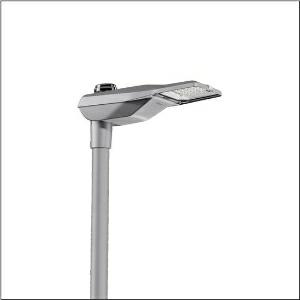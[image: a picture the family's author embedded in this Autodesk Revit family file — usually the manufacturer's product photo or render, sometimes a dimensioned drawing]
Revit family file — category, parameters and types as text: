
# Revit family: streetlight_sl_21_micro___st1_5a_5xe5p47n08cb_4c70
name_source: partatom
category: Lighting Fixtures
units: mm (PartAtom-declared; Revit-internal decimal feet)

## family parameters
Cut with Voids When Loaded = No
Host = Face
Light Source = No
Part Type = Normal
Room Calculation Point = No
Round Connector Dimension = Use Diameter
Shared = No

## types (1)
- --- (1 x LED, 2340 lm, 15.8 W, 4000K)
    Apparent Load = 16 VA
    CIE Flux Codes = 22 53 95 100 100
    Color Rendering = 70
    Color Temperature = 4000K
    Default Elevation = 1800 mm
    Description = Streetlight SL 21 micro, mast luminaire, primary light control with lens, of PMMA, primary optical cover: cover, of toughened safety glass, transparent, light distribution: ST1.5a, light emission: direct distribution, primary light characteristic: asymmetric, installation type: post-top, LED, 3G 1.5mm², High Power LED, rated luminous flux: 2.340lm, luminous efficacy: 148lm/W, light colour: 740, colour temperature: 4000K, control gear: NEMA (7pin), control: overheat protection, pre-setting: linear dimming characteristic, constant luminous flux control, time-dependent luminous flux control, flexible luminous flux parameterisation, mains connection: 230..240V, AC, 50/60Hz, connection cable pre-assembled, cable length: 6,5m, wiring characteristics: H07RN-F, start of lifetime: 16W, end of service life: 16W, reduction: 8W, luminaire housing, of diecast aluminium (EN AC-44300), powder-coated, SITECO metallic grey (DB 702S), corrosivity category C5 high according to DIN EN ISO 12944, multi-level sealing system, sealing non-destructively replaceable, inclination adjustable: 0°, 5°, 10°, 15°, length: 528mm, width: 235mm, height: 110mm, spigot size: 76/60mm (post-top), mounting height: 4..8m, protection rating (complete): IP66, insulation class (complete): insulation class I (protective earthing), certification: CE, ENEC, ENEC+, VDE, impact resistance: IK10, permissible operating ambient temperature for outdoor applications: -40..+50°C, standard-compliant lighting for roads and squares, packaging unit: 1 piece

Light Distribution: ST1.5a
    Height = 110 mm
    Lamp = 1 x LED
    Lamp Light Flux = 2340 lm
    Lamp Power = 15.8 W
    Lamp count = 1
    Length = 528 mm
    Luminous efficacy = 148 lm/W
    Manufacturer = Siteco
    ModVariant = No
    Model = 5XE5P47N08CB
    Number of Poles = 1
    OnlyDefault = Yes
    Power Factor = 1
    Product Name = Streetlight SL 21 micro | ST1.5a
    Product group = mast luminaire | pylon top
    ProductGroupID = 6100
    Protection Class = Protection class I
    Protection Degree = IP 66
    RLX_Detail_Level = 1
    RLX_Emergency_Light_Flux = 0 lm
    RLX_Emergency_Type = 0
    RLX_Emergency_Type_DB = No
    RlxData = <blob elided: 103069 chars, md5=923616bc>
    Socket = socket
    Standby Power = 0 W
    System Light Flux = 2340 lm
    System Power = 16 W
    Type Comments = factory setting: luminous flux: 100 % | dim-lin: 254 | 300 mA
    Type Image = l_1294375.jpg
    URL = http://relux.com
    VarID = @adj_133229
    Voltage = 0 V
    Weight = 0.00 kg
    Width = 235 mm

## geometry (parser evidence)
native form markers: Blend x4, Sweep x11
no freeform markers — native parametric forms only
